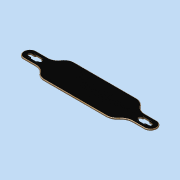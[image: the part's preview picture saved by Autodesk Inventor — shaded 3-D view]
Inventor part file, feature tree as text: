
AUTODESK INVENTOR PART (.ipt)
format: ipt  version: 2015 (Build 190159000, 159)  size: 651,264 bytes
history: native  units: mm
features: extrude x5, sketch x5, fillet x2
ambient origin geometry x8: Origin, YZ Plane, XZ Plane, XY Plane, X Axis, Y Axis, Z Axis, Center Point
bodies: Volumenkörper1 (feature_tree)
feature tree (12):
  extrude  "Extrusion1"  Depth=70.0mm TaperAngle=0.0deg
  extrude  "Extrusion2"  Depth=25.0mm
  extrude  "Extrusion3"  Depth=12.0mm
  extrude  "Extrusion4"  Depth=2000.0mm TaperAngle=0.0deg
  extrude  "Extrusion5"  Depth=5.0mm
  fillet  "Rundung1"  Radius=220.0mm
  fillet  "Rundung2"  Radius=2000.0mm
  sketch  "Skizze1"  dims[d0=70.0mm d1=0.0mm d2=70.0mm d3=0.0mm]
  sketch  "Skizze2"  dims[d4=25.0mm d5=25.0mm]
  sketch  "Skizze3"  dims[d6=220.0mm d7=12.0mm]
  sketch  "Skizze5"  dims[d8=25.0mm d9=2000.0mm d10=0.0mm]
  sketch  "Skizze6"  dims[d11=12.0mm d12=13.0mm d13=220.0mm d14=2000.0mm d15=0.0mm d16=199.5mm d17=0.0mm d18=5.0mm d19=5.0mm d20=46.0mm d21=241.3mm]
